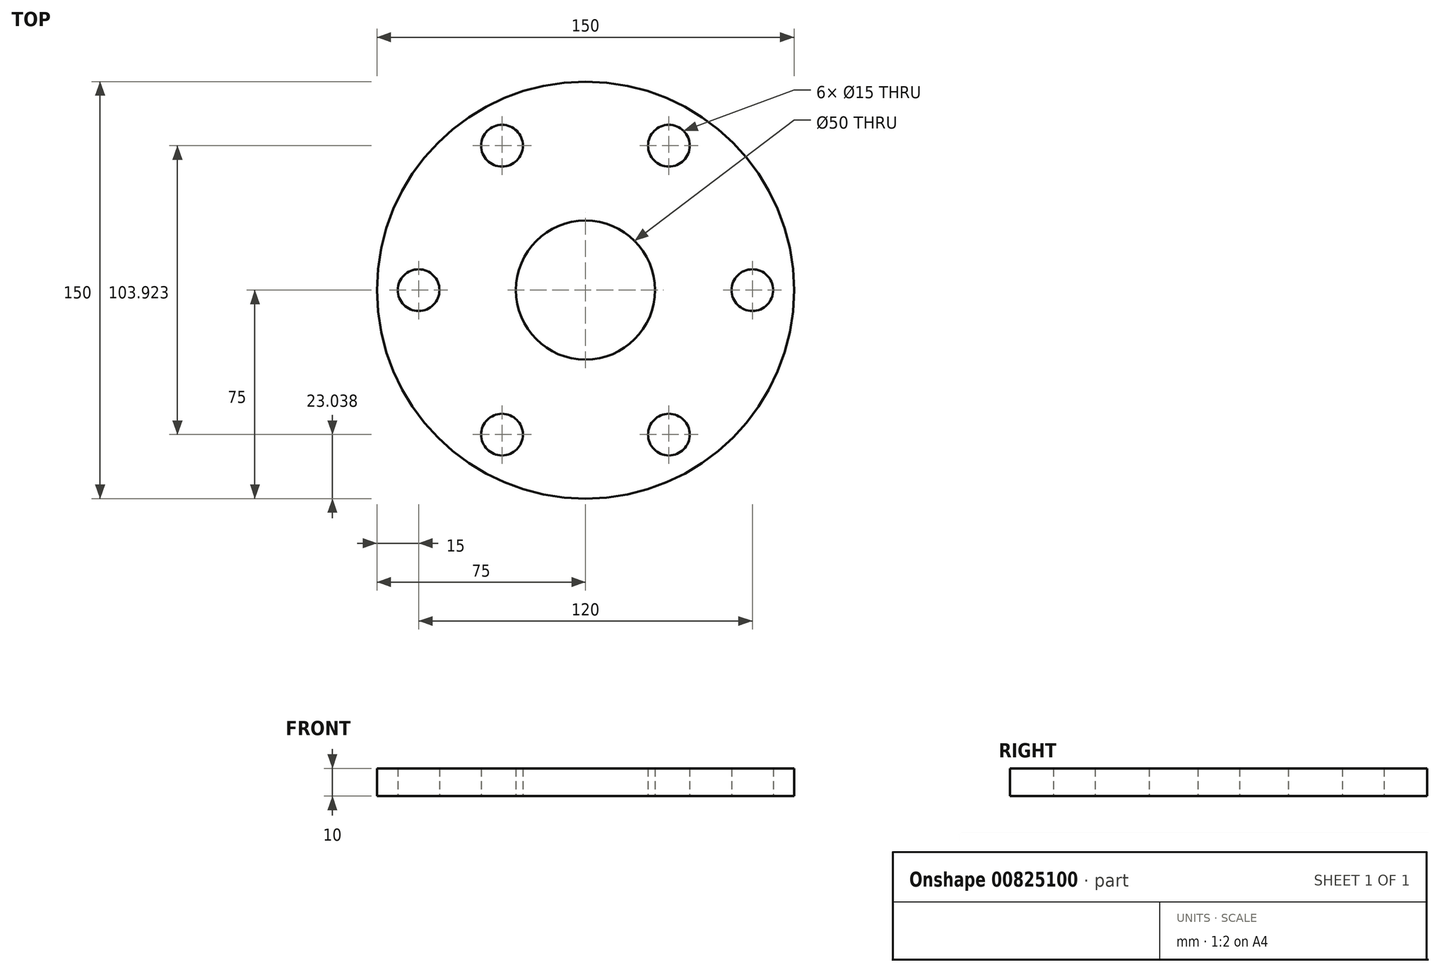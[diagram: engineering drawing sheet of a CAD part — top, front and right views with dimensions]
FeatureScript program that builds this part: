
annotation { "Feature Type Name" : "Feature", "Feature Type Description" : "" }
export const myFeature = defineFeature(function(context is Context, id is Id, definition is map)
    precondition{}
    {
        {
            var Q0;
            Q0=qCreatedBy(makeId("Top.planeOp"),FACE);
            var sketch = newSketch(context, id + "F0", { "sketchPlane" : qUnion([Q0])});
            skCircle(sketch, "E0", {"center": v(0, 0) * mm, "radius": 75 * mm});
            skCircle(sketch, "E1", {"center": v(0, 0) * mm, "radius": 25 * mm});
            skSolve(sketch);
        }
        {
            var Q0;
            Q0=makeQuery(id+"F0.imprint","IMPRINT",FACE,{"disambiguationData":[TD([[makeQuery(id+"F0.imprint","IMPRINT",EDGE,{"derivedFrom":sQuery(id+"F0.wireOp",EDGE,"E0")}),1.0]])]});
            extrude(context, id + "F1", {"entities" : qUnion([Q0]), "depth" : 10 * mm, "offsetDistance" : 25 * mm});
        }
        {
            var Q0;
            Q0=qCreatedBy(makeId("Top.planeOp"),FACE);
            var sketch = newSketch(context, id + "F2", { "sketchPlane" : qUnion([Q0])});
            skCircle(sketch, "E2", {"center": v(60, 0) * mm, "radius": 7.5 * mm});
            skCircle(sketch, "E3.1.0", {"center": v(30, 51.96) * mm, "radius": 7.5 * mm});
            skCircle(sketch, "E3.2.0", {"center": v(-30, 51.96) * mm, "radius": 7.5 * mm});
            skCircle(sketch, "E3.3.0", {"center": v(-60, 0) * mm, "radius": 7.5 * mm});
            skCircle(sketch, "E3.4.0", {"center": v(-30, -51.96) * mm, "radius": 7.5 * mm});
            skCircle(sketch, "E3.5.0", {"center": v(30, -51.96) * mm, "radius": 7.5 * mm});
            skPoint(sketch, "E3.center", {"position": v(0, 0) * mm});
            skSolve(sketch);
        }
        {
            var Q0;
            Q0 = qSketchRegion(id + "F2", true);
            extrude(context, id + "F3", {"entities" : qUnion([Q0]), "operationType" : NewBodyOperationType.REMOVE, "depth" : 25 * mm, "offsetDistance" : 25 * mm});
        }
    });
